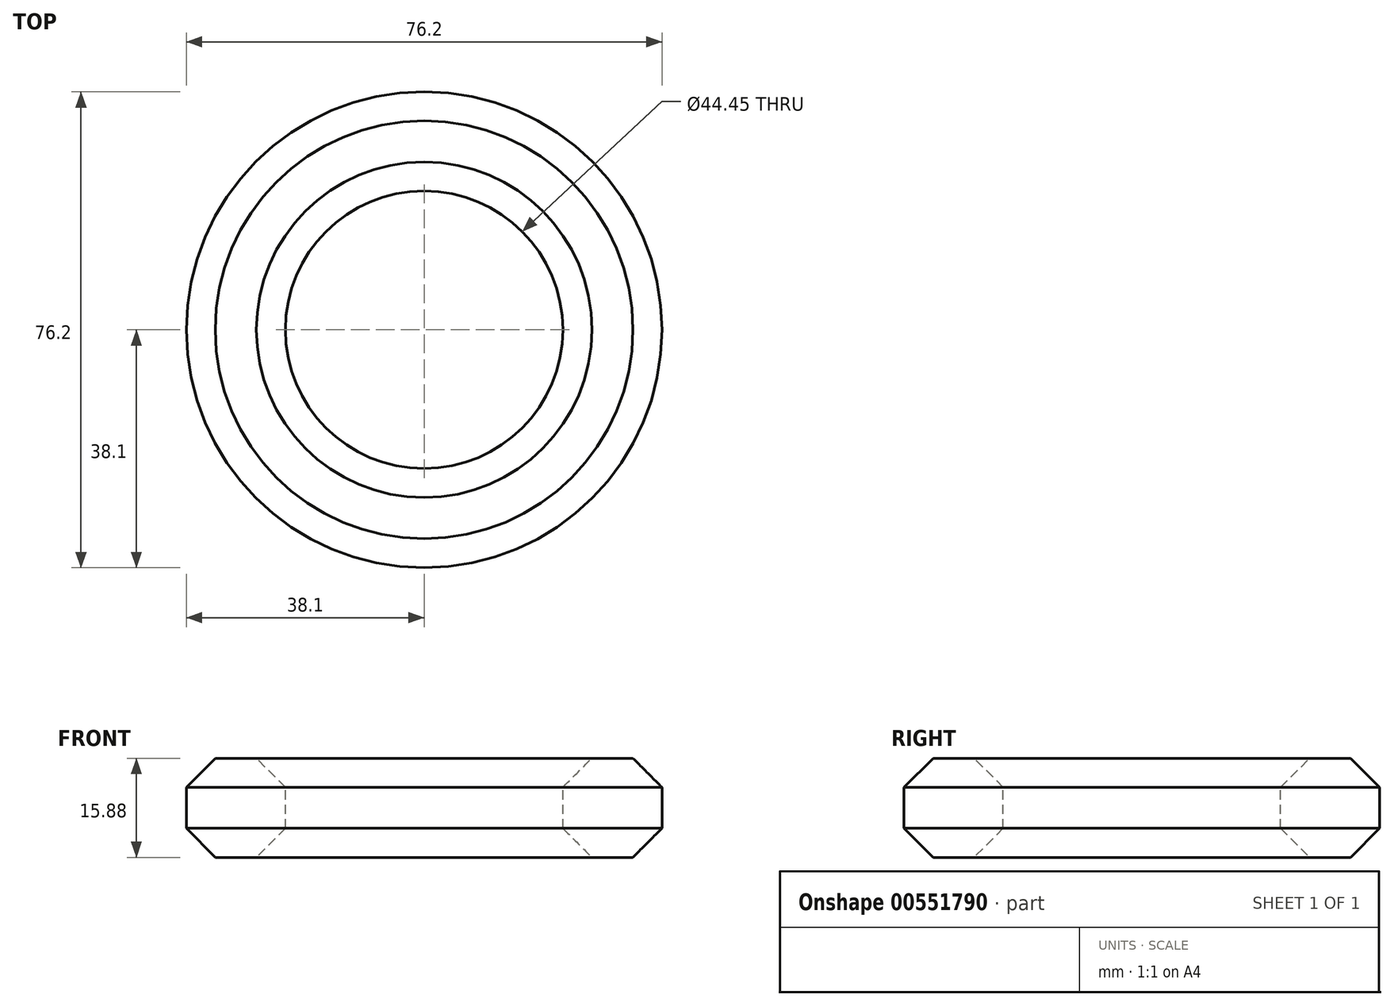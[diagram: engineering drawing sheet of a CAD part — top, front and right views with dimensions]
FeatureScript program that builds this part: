
annotation { "Feature Type Name" : "Feature", "Feature Type Description" : "" }
export const myFeature = defineFeature(function(context is Context, id is Id, definition is map)
    precondition{}
    {
        {
            var Q0;
            Q0=qCreatedBy(makeId("Top.planeOp"),FACE);
            var sketch = newSketch(context, id + "F0", { "sketchPlane" : qUnion([Q0])});
            skCircle(sketch, "E0", {"center": v(0, 0) * mm, "radius": 30.16 * mm});
            skSolve(sketch);
        }
        {
            var Q0;
            Q0=qCreatedBy(makeId("Front.planeOp"),FACE);
            var sketch = newSketch(context, id + "F1", { "sketchPlane" : qUnion([Q0])});
            skLineSegment(sketch, "E1.0", {"start": v(-30.16, 0) * mm, "end": v(30.16, 0) * mm, "construction": true});
            skCircle(sketch, "E2.cCircle", {"center": v(30.16, 0) * mm, "radius": 7.94 * mm, "construction": true});
            skLineSegment(sketch, "E2.0", {"start": v(33.45, -7.94) * mm, "end": v(26.87, -7.94) * mm});
            skLineSegment(sketch, "E2.1", {"start": v(26.87, -7.94) * mm, "end": v(22.23, -3.29) * mm});
            skLineSegment(sketch, "E2.2", {"start": v(22.23, -3.29) * mm, "end": v(22.23, 3.29) * mm});
            skLineSegment(sketch, "E2.3", {"start": v(22.22, 3.29) * mm, "end": v(26.87, 7.94) * mm});
            skLineSegment(sketch, "E2.4", {"start": v(26.87, 7.94) * mm, "end": v(33.45, 7.94) * mm});
            skLineSegment(sketch, "E2.5", {"start": v(33.45, 7.94) * mm, "end": v(38.1, 3.29) * mm});
            skLineSegment(sketch, "E2.6", {"start": v(38.1, 3.29) * mm, "end": v(38.1, -3.29) * mm});
            skLineSegment(sketch, "E2.7", {"start": v(38.1, -3.29) * mm, "end": v(33.45, -7.94) * mm});
            skPoint(sketch, "E2.0.midPoint", {"position": v(30.16, -7.94) * mm});
            skSolve(sketch);
        }
        {
            var Q0;
            Q0=makeQuery(id+"F1.imprint","IMPRINT",FACE,{"disambiguationData":[TD([[makeQuery(id+"F1.imprint","IMPRINT",EDGE,{"derivedFrom":sQuery(id+"F1.wireOp",EDGE,"E2.0")}),-1.0]])]});
            var Q1;
            Q1=sQuery(id+"F0.wireOp",EDGE,"E0");
            sweep(context, id + "F2", {"profiles" : qUnion([Q0]), "path" : qUnion([Q1])});
        }
    });
